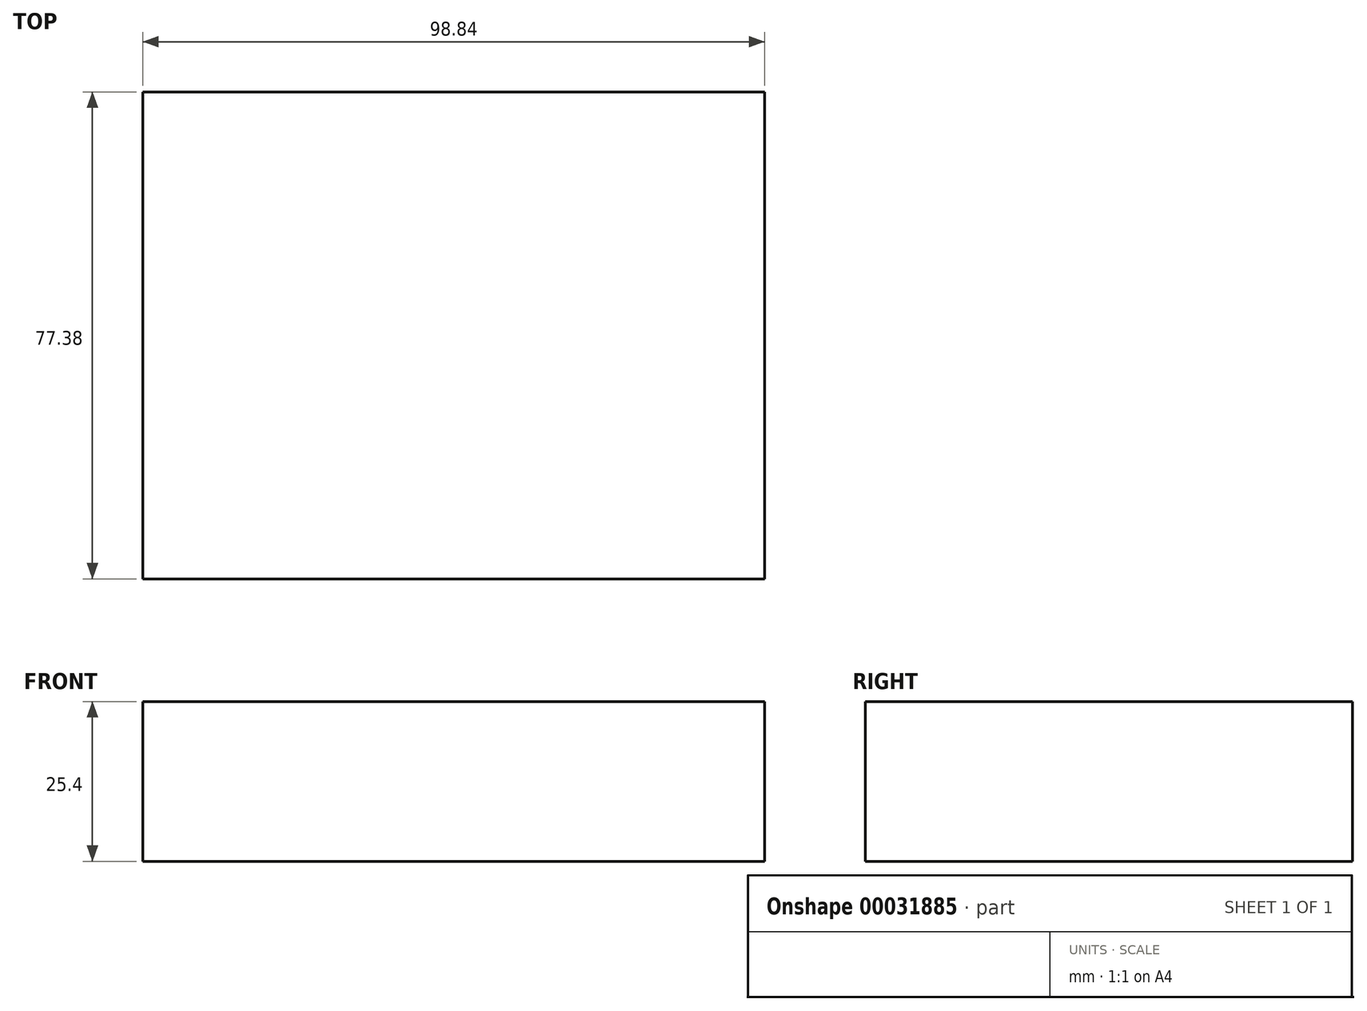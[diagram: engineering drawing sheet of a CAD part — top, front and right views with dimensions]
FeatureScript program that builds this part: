
annotation { "Feature Type Name" : "Feature", "Feature Type Description" : "" }
export const myFeature = defineFeature(function(context is Context, id is Id, definition is map)
    precondition{}
    {
        {
            var Q0;
            Q0=qCreatedBy(makeId("Top.planeOp"),FACE);
            var sketch = newSketch(context, id + "F0", { "sketchPlane" : qUnion([Q0])});
            skLineSegment(sketch, "E0.rect.bottom", {"start": v(-49.42, 38.69) * mm, "end": v(49.42, 38.69) * mm});
            skLineSegment(sketch, "E0.rect.top", {"start": v(-49.42, -38.69) * mm, "end": v(49.42, -38.69) * mm});
            skLineSegment(sketch, "E0.rect.left", {"start": v(-49.42, 38.69) * mm, "end": v(-49.42, -38.69) * mm});
            skLineSegment(sketch, "E0.rect.right", {"start": v(49.42, 38.69) * mm, "end": v(49.42, -38.69) * mm});
            skPoint(sketch, "E0.rect.middle", {"position": v(0, 0) * mm});
            skSolve(sketch);
        }
        {
            var Q0;
            Q0 = qSketchRegion(id + "F0", true);
            extrude(context, id + "F1", {"entities" : qUnion([Q0]), "depth" : 25.4 * mm});
        }
    });
